FCSTD DOCUMENT  (FreeCAD 1.0R39109 (Git))
Label: Self Tap screw sketches
License: All rights reserved
LicenseURL: https://en.wikipedia.org/wiki/All_rights_reserved
objects: Sketcher::SketchObject×3
note: 6 computed .brp shape members not serialized (recipe doc carries the construction recipe); baked Part::Feature solids carry a one-line shape summary decoded from their .brp

FEATURE [Sketcher::SketchObject] Sketch  label="M3 self tap Sketch"
  ArcFitTolerance = 1e-06
  FullyConstrained = false
  MakeInternals = false
  MapMode = 5
  expr: Constraints[19] = .Constraints.Holeradius * 2 + 0.9 mm
  expr: Constraints[22] = .Constraints.Holeradius / 2
  sketch-geometry (10):
    g0: ArcOfCircle CenterX=-0.517439 CenterY=0.767765 CenterZ=0 NormalX=0 NormalY=0 NormalZ=1 AngleXU=0 Radius=1.6 StartAngle=0.890878 EndAngle=2.25072
    g1: ArcOfCircle CenterX=1.25791 CenterY=1.79277 CenterZ=0 NormalX=0 NormalY=0 NormalZ=1 AngleXU=0 Radius=0.8 StartAngle=2.86405 EndAngle=4.46634
    g2: ArcOfCircle CenterX=-0.517439 CenterY=0.767765 CenterZ=0 NormalX=0 NormalY=0 NormalZ=1 AngleXU=0 Radius=1.6 StartAngle=5.07967 EndAngle=6.43951
    g3: ArcOfCircle CenterX=-0.517439 CenterY=-1.28224 CenterZ=0 NormalX=0 NormalY=0 NormalZ=1 AngleXU=0 Radius=0.8 StartAngle=0.76965 EndAngle=2.37194
    g4: ArcOfCircle CenterX=-0.517439 CenterY=0.767765 CenterZ=0 NormalX=0 NormalY=0 NormalZ=1 AngleXU=0 Radius=1.6 StartAngle=2.98527 EndAngle=4.34511
    g5: ArcOfCircle CenterX=-2.29279 CenterY=1.79277 CenterZ=0 NormalX=0 NormalY=0 NormalZ=1 AngleXU=0 Radius=0.8 StartAngle=4.95844 EndAngle=6.56073
    g6: LineSegment [constr] StartX=1.25791 StartY=1.79277 StartZ=0 EndX=-2.29279 EndY=1.79277 EndZ=0
    g7: LineSegment [constr] StartX=-2.29279 StartY=1.79277 StartZ=0 EndX=-0.517439 EndY=-1.28224 EndZ=0
    g8: LineSegment [constr] StartX=-0.517439 StartY=-1.28224 StartZ=0 EndX=1.25791 EndY=1.79277 EndZ=0
    g9: Circle [constr] CenterX=-0.517439 CenterY=0.767765 CenterZ=0 NormalX=0 NormalY=0 NormalZ=1 AngleXU=0 Radius=2.05
  constraints (28):
    c: Coincident(g1,g0)
    c: Coincident(g2,g1)
    c: Coincident(g3,g2)
    c: Coincident(g4,g3)
    c: Coincident(g5,g4)
    c: Coincident(g5,g0)
    c: Equal(g0,g2)
    c: Equal(g2,g4)
    c: Coincident(g6,g7)
    c: Coincident(g7,g8)
    c: Coincident(g8,g6)
    c: Equal(g6,g7)
    c: Equal(g6,g8)
    c: PointOnObject(g6,g9)
    c: PointOnObject(g7,g9)
    c: PointOnObject(g8,g9)
    c: Coincident(g9,g0)
    c: Coincident(g8,g1)
    c: Radius(g0) = 1.6  'Holeradius'
    c: Diameter(g9) = 4.1
    c: Equal(g3,g1)
    c: Equal(g1,g5)
    c: Radius(g5) = 0.8
    c: Coincident(g0,g2)
    c: Coincident(g0,g4)
    c: Coincident(g6,g5)
    c: Coincident(g3,g7)
    c: Horizontal(g6)
FEATURE [Sketcher::SketchObject] Sketch001  label="M5 self tap Sketch"
  ArcFitTolerance = 1e-06
  FullyConstrained = false
  MakeInternals = false
  MapMode = 5
  expr: Constraints[19] = .Constraints.Holeradius * 2 + 0.9 mm
  expr: Constraints[22] = .Constraints.Holeradius / 2
  sketch-geometry (10):
    g0: ArcOfCircle CenterX=-0.399388 CenterY=0.217094 CenterZ=0 NormalX=0 NormalY=0 NormalZ=1 AngleXU=0 Radius=2.6 StartAngle=0.960161 EndAngle=2.18143
    g1: ArcOfCircle CenterX=2.24199 CenterY=1.74209 CenterZ=0 NormalX=0 NormalY=0 NormalZ=1 AngleXU=0 Radius=1.3 StartAngle=2.6574 EndAngle=4.67298
    g2: ArcOfCircle CenterX=-0.399388 CenterY=0.217094 CenterZ=0 NormalX=0 NormalY=0 NormalZ=1 AngleXU=0 Radius=2.6 StartAngle=5.14895 EndAngle=6.37022
    g3: ArcOfCircle CenterX=-0.399388 CenterY=-2.83291 CenterZ=0 NormalX=0 NormalY=0 NormalZ=1 AngleXU=0 Radius=1.3 StartAngle=0.563008 EndAngle=2.57858
    g4: ArcOfCircle CenterX=-0.399388 CenterY=0.217094 CenterZ=0 NormalX=0 NormalY=0 NormalZ=1 AngleXU=0 Radius=2.6 StartAngle=3.05456 EndAngle=4.27583
    g5: ArcOfCircle CenterX=-3.04077 CenterY=1.74209 CenterZ=0 NormalX=0 NormalY=0 NormalZ=1 AngleXU=0 Radius=1.3 StartAngle=4.7518 EndAngle=6.76737
    g6: LineSegment [constr] StartX=2.24199 StartY=1.74209 StartZ=0 EndX=-3.04077 EndY=1.74209 EndZ=0
    g7: LineSegment [constr] StartX=-3.04077 StartY=1.74209 StartZ=0 EndX=-0.399388 EndY=-2.83291 EndZ=0
    g8: LineSegment [constr] StartX=-0.399388 StartY=-2.83291 StartZ=0 EndX=2.24199 EndY=1.74209 EndZ=0
    g9: Circle [constr] CenterX=-0.399388 CenterY=0.217094 CenterZ=0 NormalX=0 NormalY=0 NormalZ=1 AngleXU=0 Radius=3.05
  constraints (28):
    c: Coincident(g1,g0)
    c: Coincident(g2,g1)
    c: Coincident(g3,g2)
    c: Coincident(g4,g3)
    c: Coincident(g5,g4)
    c: Coincident(g5,g0)
    c: Equal(g0,g2)
    c: Equal(g2,g4)
    c: Coincident(g6,g7)
    c: Coincident(g7,g8)
    c: Coincident(g8,g6)
    c: Equal(g6,g7)
    c: Equal(g6,g8)
    c: PointOnObject(g6,g9)
    c: PointOnObject(g7,g9)
    c: PointOnObject(g8,g9)
    c: Coincident(g9,g0)
    c: Coincident(g8,g1)
    c: Radius(g0) = 2.6  'Holeradius'
    c: Diameter(g9) = 6.1
    c: Equal(g3,g1)
    c: Equal(g1,g5)
    c: Radius(g5) = 1.3
    c: Coincident(g0,g2)
    c: Coincident(g0,g4)
    c: Coincident(g6,g5)
    c: Coincident(g3,g7)
    c: Horizontal(g6)
FEATURE [Sketcher::SketchObject] Sketch002  label="M4 self tap Sketch"
  ArcFitTolerance = 1e-06
  FullyConstrained = false
  MakeInternals = false
  MapMode = 5
  expr: Constraints[19] = .Constraints.Holeradius * 2 + 0.9 mm
  expr: Constraints[22] = .Constraints.Holeradius / 2
  sketch-geometry (10):
    g0: ArcOfCircle CenterX=-0.428062 CenterY=0.51399 CenterZ=0 NormalX=0 NormalY=0 NormalZ=1 AngleXU=0 Radius=2.1 StartAngle=0.936485 EndAngle=2.20511
    g1: ArcOfCircle CenterX=1.7803 CenterY=1.78899 CenterZ=0 NormalX=0 NormalY=0 NormalZ=1 AngleXU=0 Radius=1.05 StartAngle=2.7337 EndAngle=4.59668
    g2: ArcOfCircle CenterX=-0.428062 CenterY=0.51399 CenterZ=0 NormalX=0 NormalY=0 NormalZ=1 AngleXU=0 Radius=2.1 StartAngle=5.12528 EndAngle=6.3939
    g3: ArcOfCircle CenterX=-0.428062 CenterY=-2.03601 CenterZ=0 NormalX=0 NormalY=0 NormalZ=1 AngleXU=0 Radius=1.05 StartAngle=0.639306 EndAngle=2.50229
    g4: ArcOfCircle CenterX=-0.428062 CenterY=0.51399 CenterZ=0 NormalX=0 NormalY=0 NormalZ=1 AngleXU=0 Radius=2.1 StartAngle=3.03088 EndAngle=4.2995
    g5: ArcOfCircle CenterX=-2.63643 CenterY=1.78899 CenterZ=0 NormalX=0 NormalY=0 NormalZ=1 AngleXU=0 Radius=1.05 StartAngle=4.8281 EndAngle=6.69108
    g6: LineSegment [constr] StartX=1.7803 StartY=1.78899 StartZ=0 EndX=-2.63643 EndY=1.78899 EndZ=0
    g7: LineSegment [constr] StartX=-2.63643 StartY=1.78899 StartZ=0 EndX=-0.428062 EndY=-2.03601 EndZ=0
    g8: LineSegment [constr] StartX=-0.428062 StartY=-2.03601 StartZ=0 EndX=1.7803 EndY=1.78899 EndZ=0
    g9: Circle [constr] CenterX=-0.428062 CenterY=0.51399 CenterZ=0 NormalX=0 NormalY=0 NormalZ=1 AngleXU=0 Radius=2.55
  constraints (28):
    c: Coincident(g1,g0)
    c: Coincident(g2,g1)
    c: Coincident(g3,g2)
    c: Coincident(g4,g3)
    c: Coincident(g5,g4)
    c: Coincident(g5,g0)
    c: Equal(g0,g2)
    c: Equal(g2,g4)
    c: Coincident(g6,g7)
    c: Coincident(g7,g8)
    c: Coincident(g8,g6)
    c: Equal(g6,g7)
    c: Equal(g6,g8)
    c: PointOnObject(g6,g9)
    c: PointOnObject(g7,g9)
    c: PointOnObject(g8,g9)
    c: Coincident(g9,g0)
    c: Coincident(g8,g1)
    c: Radius(g0) = 2.1  'Holeradius'
    c: Diameter(g9) = 5.1
    c: Equal(g3,g1)
    c: Equal(g1,g5)
    c: Radius(g5) = 1.05
    c: Coincident(g0,g2)
    c: Coincident(g0,g4)
    c: Coincident(g6,g5)
    c: Coincident(g3,g7)
    c: Horizontal(g6)
